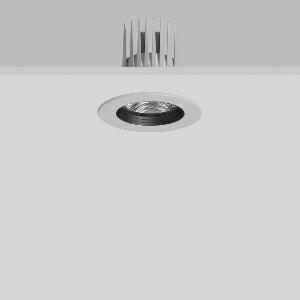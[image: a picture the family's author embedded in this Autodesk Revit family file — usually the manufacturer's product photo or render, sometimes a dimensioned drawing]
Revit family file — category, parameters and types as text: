
# Revit family: heledon_mini_e_901749_004_9bf9
name_source: partatom
category: Lighting Fixtures
units: mm (PartAtom-declared; Revit-internal decimal feet)

## family parameters
Cut with Voids When Loaded = No
Host = Face
Light Source = No
Part Type = Normal
Room Calculation Point = No
Round Connector Dimension = Use Diameter
Shared = No

## types (1)
- HELEDON mini E (1 x LED Modul 930, 3500 lm, 3000)
    Apparent Load = 29 VA
    Approval mark = CE
    CIE Flux Codes = 99 100 100 100 100
    Color Rendering = 90
    Color Temperature = 3000
    Default Elevation = 1800 mm
    Description = Series: HELEDON mini
Round recessed downlight. Housing: die-cast aluminium, powder-coated. Black plastic ring and recessed LED to prevent glare from the side. Optical assembly with reflector made of MIRO-Silver with 98% total light reflection for outstanding efficiency - can be changed without tools. Best colour rendering index Ra>90. Suitable for Recessed ceiling mounting. Installation without tools thanks to spring fastening system. Including separate LED converter with connecting cable 600 mm.High quality converter without flickering and stroboscopic effect. Through-wiring box (5 pole) available as accessory. The following accessories can be mounted without use of tools: interchangeable lenses, decorative glasses, honeycomb louvre, clear and frosted diffusers, white interchangeable plastic ring. 
Colour: silver
Diameter: 124 mm
Height: 3 mm
Cut-out diameter: 114 mm
Recess height: 170 mm
Luminaire: recess height: 120 mm
Lamp: LED
Socket: without socket
Colour temperature: 3000K
Colour rendering index (CRI): 92
System power: 29 W
Rated luminous flux: 3500 lm
Luminous efficiency: 121 lm/W
Control gear: Regulated power supply
Protection class: II
Type of protection: IP 20
    Height = 0 mm  [stored 0 ft]
    Lamp = 1 x LED Modul 930
    Lamp Light Flux = 3500 lm
    Lamp count = 1
    Length = 124 mm  [stored 0.406824 ft]
    Lifetime = 50000 h
    Luminous efficacy = 121 lm/W
    Manufacturer = RZB
    ModVariant = No
    Model = 901749.004
    Mounting Place = Ceiling
    Mounting Type = Recessed
    Number of Poles = 1
    OnlyDefault = Yes
    Power Factor = 1
    Product Name = HELEDON mini E
    Product group = Recessed downlights
    ProductGroupID = 402
    Protection Class = Protection class II
    Protection Degree = IP 20
    RLX_Detail_Level = 1
    RLX_Emergency_Light_Flux = 0 lm
    RLX_Emergency_Type = 0
    RLX_Emergency_Type_DB = No
    RlxData = <blob elided: 128777 chars, md5=fb3d3655>
    Socket = socket
    Standby Power = 0 W
    System Light Flux = 3500 lm
    System Power = 29 W
    Type Comments = Product without accessories
    Type Image = 901657.004.jpg
    URL = http://relux.com
    VarID = ---
    Voltage = 230 V
    Voltage Range = 220-240 V
    Weight = 0.00 kg
    Width = 0 mm  [stored 0 ft]

note: [stored X ft] marks values corroborated as IEEE doubles in the binary element streams (Revit-internal decimal feet)

## geometry (parser evidence)
native form markers: Blend x4, Sweep x9
no freeform markers — native parametric forms only
